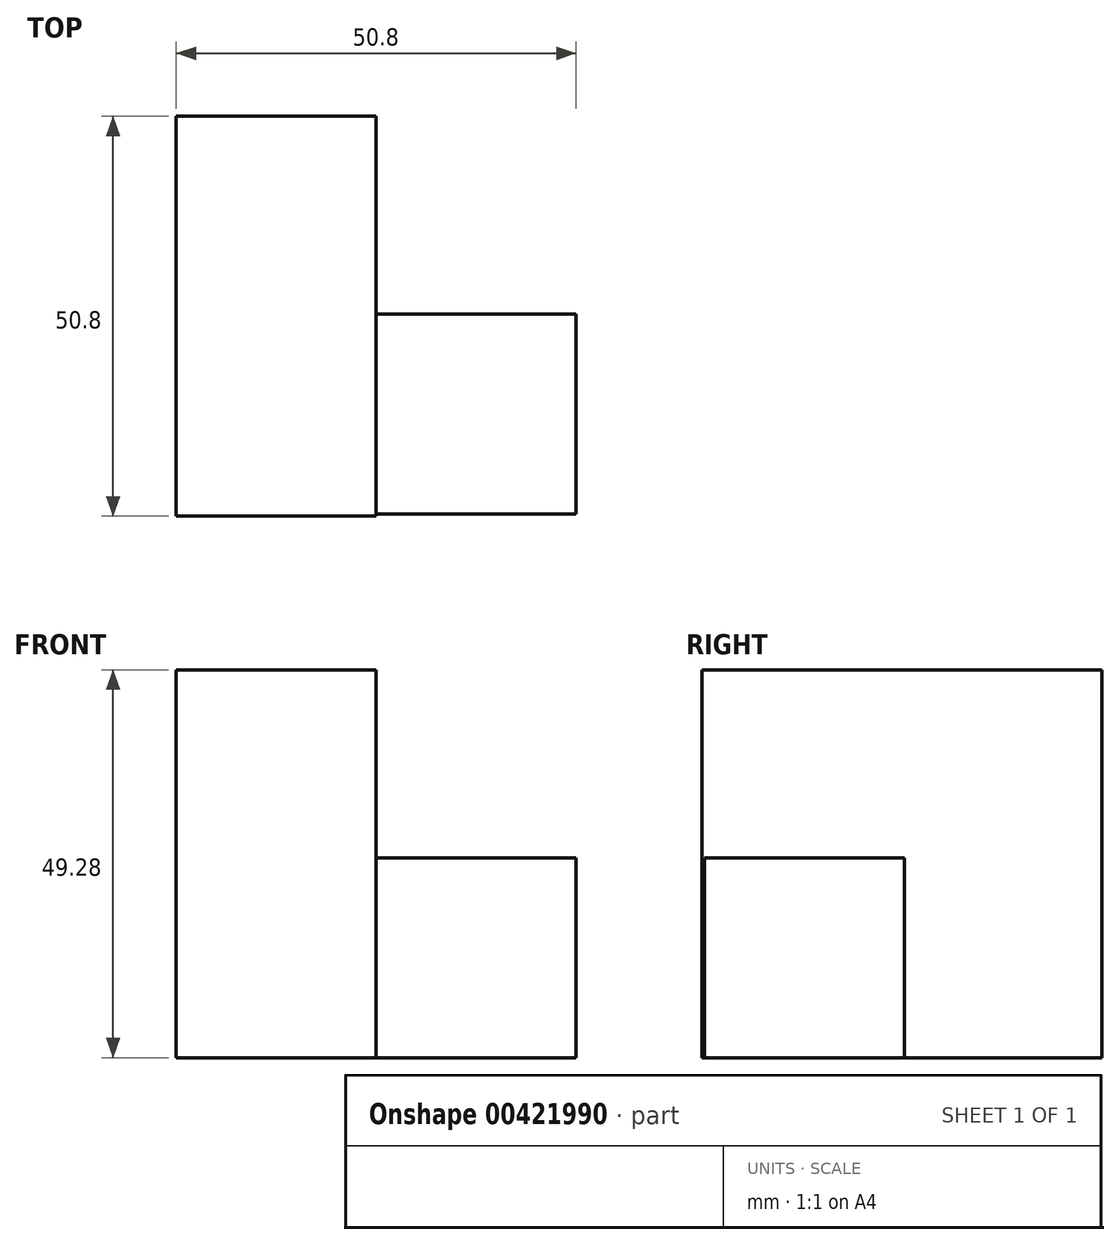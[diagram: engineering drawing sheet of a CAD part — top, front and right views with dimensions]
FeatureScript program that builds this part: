
annotation { "Feature Type Name" : "Feature", "Feature Type Description" : "" }
export const myFeature = defineFeature(function(context is Context, id is Id, definition is map)
    precondition{}
    {
        {
            var Q0;
            Q0=qCreatedBy(makeId("Front.planeOp"),FACE);
            var sketch = newSketch(context, id + "F0", { "sketchPlane" : qUnion([Q0])});
            skLineSegment(sketch, "E0", {"start": v(0, -1.52) * mm, "end": v(0, 49.28) * mm});
            skLineSegment(sketch, "E1", {"start": v(0, 49.28) * mm, "end": v(-25.4, 49.28) * mm});
            skLineSegment(sketch, "E2", {"start": v(-25.4, 49.28) * mm, "end": v(-25.4, 0) * mm});
            skLineSegment(sketch, "E3", {"start": v(-25.4, 0) * mm, "end": v(0, 0) * mm});
            skSolve(sketch);
        }
        {
            var Q0;
            Q0 = qSketchRegion(id + "F0", true);
            extrude(context, id + "F1", {"entities" : qUnion([Q0]), "depth" : 50.8 * mm});
        }
        {
            var Q0;
            Q0=qCreatedBy(makeId("Right.planeOp"),FACE);
            var sketch = newSketch(context, id + "F2", { "sketchPlane" : qUnion([Q0])});
            skLineSegment(sketch, "E4.bottom", {"start": v(-50.53, 0) * mm, "end": v(-25.13, 0) * mm});
            skLineSegment(sketch, "E4.top", {"start": v(-50.53, 25.4) * mm, "end": v(-25.13, 25.4) * mm});
            skLineSegment(sketch, "E4.left", {"start": v(-50.53, 0) * mm, "end": v(-50.53, 25.4) * mm});
            skLineSegment(sketch, "E4.right", {"start": v(-25.13, 0) * mm, "end": v(-25.13, 25.4) * mm});
            skSolve(sketch);
        }
        {
            var Q0;
            Q0 = qSketchRegion(id + "F2", true);
            extrude(context, id + "F3", {"entities" : qUnion([Q0]), "operationType" : NewBodyOperationType.ADD, "depth" : 25.4 * mm});
        }
    });
